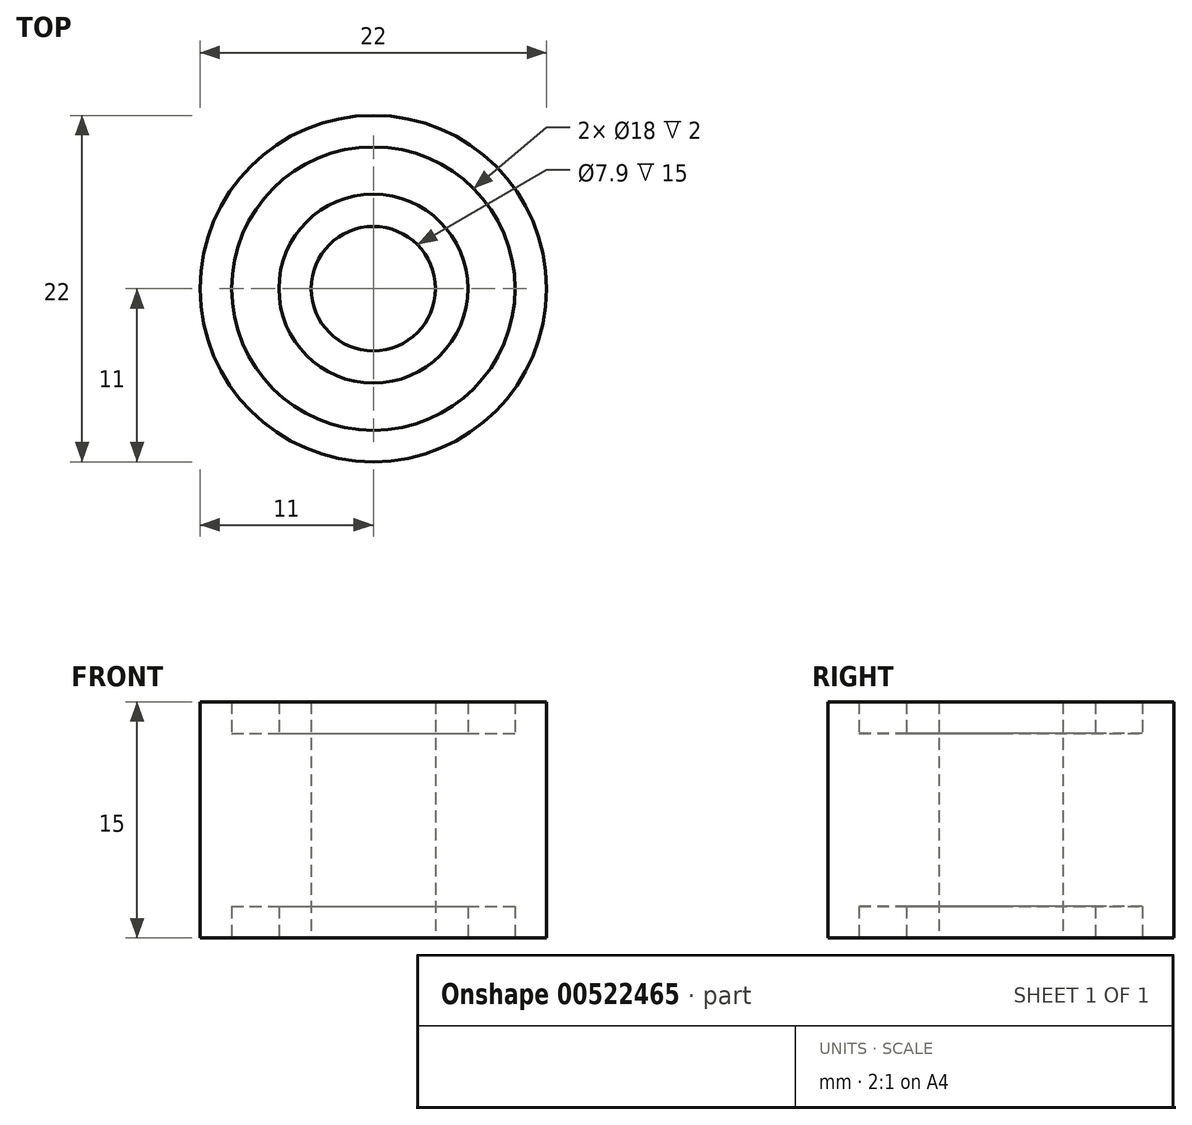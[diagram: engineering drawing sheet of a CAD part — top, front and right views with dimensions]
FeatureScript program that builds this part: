
annotation { "Feature Type Name" : "Feature", "Feature Type Description" : "" }
export const myFeature = defineFeature(function(context is Context, id is Id, definition is map)
    precondition{}
    {
        {
            var Q0;
            Q0=qCreatedBy(makeId("Front.planeOp"),FACE);
            var sketch = newSketch(context, id + "F0", { "sketchPlane" : qUnion([Q0])});
            skLineSegment(sketch, "E0.bottom", {"start": v(0, 0) * mm, "end": v(-6, 0) * mm});
            skLineSegment(sketch, "E0.top", {"start": v(-3.95, 15) * mm, "end": v(-6, 15) * mm});
            skLineSegment(sketch, "E0.left", {"start": v(0, 0) * mm, "end": v(0, 15) * mm, "construction": true});
            skLineSegment(sketch, "E0.right", {"start": v(-11, 0) * mm, "end": v(-11, 15) * mm});
            skLineSegment(sketch, "E1.bottom", {"start": v(-11, 15) * mm, "end": v(-9, 15) * mm});
            skLineSegment(sketch, "E1.left", {"start": v(-11, 15) * mm, "end": v(-11, 13) * mm});
            skLineSegment(sketch, "E1.right", {"start": v(-9, 15) * mm, "end": v(-9, 13) * mm});
            skLineSegment(sketch, "E2.left", {"start": v(-3.95, 15) * mm, "end": v(-3.95, 13) * mm});
            skLineSegment(sketch, "E2.right", {"start": v(-6, 15) * mm, "end": v(-6, 13) * mm});
            skLineSegment(sketch, "E3", {"start": v(-9, 13) * mm, "end": v(-6, 13) * mm});
            skLineSegment(sketch, "E4", {"start": v(-9, 2) * mm, "end": v(-9, 0) * mm});
            skLineSegment(sketch, "E5", {"start": v(-6, 2) * mm, "end": v(-6, 0) * mm});
            skLineSegment(sketch, "E6", {"start": v(-3.95, 13) * mm, "end": v(-3.95, 0) * mm});
            skPoint(sketch, "E7", {"position": v(-9, 2) * mm});
            skPoint(sketch, "E8", {"position": v(-6, 2) * mm});
            skLineSegment(sketch, "E9", {"start": v(-6, 2) * mm, "end": v(-9, 2) * mm});
            skLineSegment(sketch, "E10.trimOffspring", {"start": v(-9, 15) * mm, "end": v(-11, 15) * mm});
            skLineSegment(sketch, "E11.trimOffspring", {"start": v(-9, 0) * mm, "end": v(-11, 0) * mm});
            skPoint(sketch, "E12.orphan", {"position": v(-3.95, 2) * mm});
            skLineSegment(sketch, "E13", {"start": v(-11, 13) * mm, "end": v(-3.95, 13) * mm, "construction": true});
            skLineSegment(sketch, "E14", {"start": v(-3.95, 2) * mm, "end": v(-11, 2) * mm, "construction": true});
            skSolve(sketch);
        }
        {
            var Q0;
            Q0=makeQuery(id+"F0.imprint","IMPRINT",FACE,{"disambiguationData":[TD([[makeQuery(id+"F0.imprint","IMPRINT",EDGE,{"derivedFrom":sQuery(id+"F0.wireOp",EDGE,"E0.top")}),1.0]])]});
            var Q1;
            Q1=sQuery(id+"F0.wireOp",EDGE,"E0.left");
            revolve(context, id + "F1", {"entities" : qUnion([Q0]), "axis" : qUnion([Q1]), "revolveType" : RevolveType.FULL});
        }
    });
